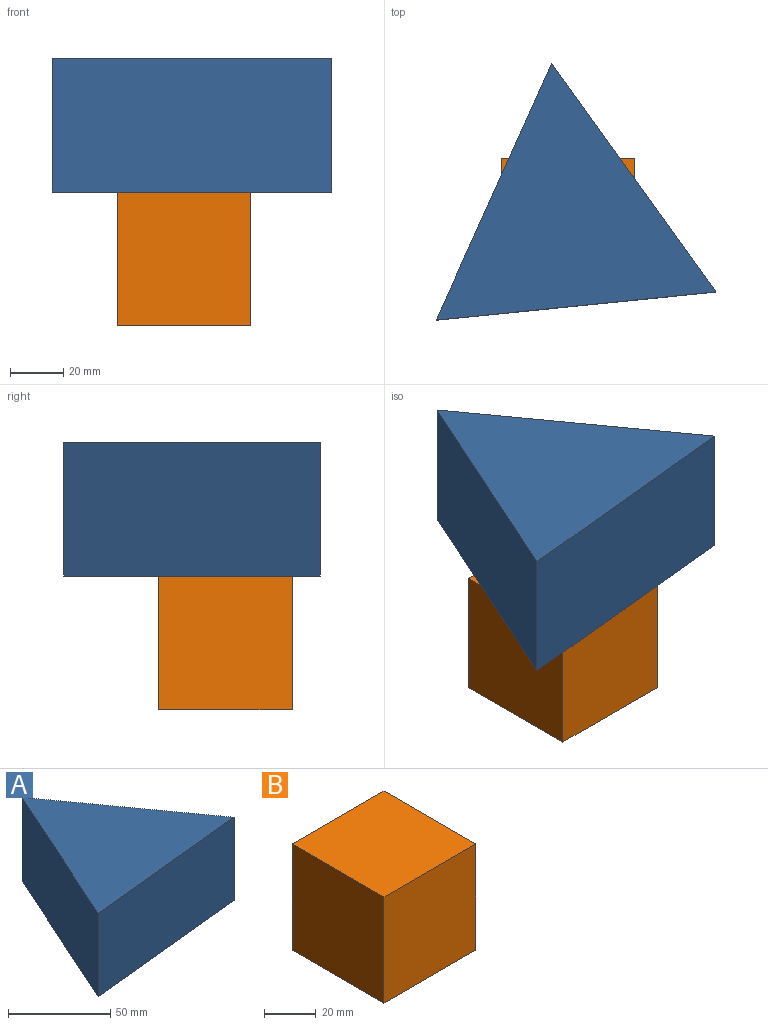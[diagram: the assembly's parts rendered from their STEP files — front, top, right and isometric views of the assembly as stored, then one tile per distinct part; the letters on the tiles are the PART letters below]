
ASSEMBLY  parts=2 mates=1
PART A: 5 faces, bbox 104.7x96x50 mm
  f0: plane 95.95x50mm, normal (-0.91,0.41,0), area 5262.2mm2, adj f1,f2,f3,f4
  f1: plane 104.72x50mm, normal (0.1,-0.99,0), area 5262.2mm2, adj f0,f2,f3,f4
  f2: plane 85.42x61.48mm, normal (0.81,0.58,0), area 5262.2mm2, adj f0,f1,f3,f4
  f3: plane 104.72x95.95mm, normal (0,0,1), area 4796.1mm2, adj f0,f1,f2
  f4: plane 104.72x95.95mm, normal (0,0,-1), area 4796.1mm2, adj f0,f1,f2
PART B: 6 faces, bbox 50x50x50 mm
  f0: plane 50x50mm, normal (-1,0,0), area 2500mm2, adj f1,f3,f4,f5
  f1: plane 50x50mm, normal (0,-1,0), area 2500mm2, adj f0,f2,f4,f5
  f2: plane 50x50mm, normal (1,0,0), area 2500mm2, adj f1,f3,f4,f5
  f3: plane 50x50mm, normal (0,1,0), area 2500mm2, adj f0,f2,f4,f5
  f4: plane 50x50mm, normal (0,0,1), area 2500mm2, adj f0,f1,f2,f3
  f5: plane 50x50mm, normal (0,0,-1), area 2500mm2, adj f0,f1,f2,f3
PLACE A t=(157.9,84.32,-10.26)mm
PLACE B t=(157.9,84.32,-35.26)mm
MATE fastened B.f4 <-> A.f4  axis (0,0,1) through (157.9,84.32,-10.26)mm
